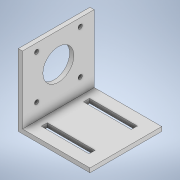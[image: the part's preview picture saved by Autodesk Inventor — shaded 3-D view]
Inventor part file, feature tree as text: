
AUTODESK INVENTOR PART (.ipt)
format: ipt  version: 2022 (Build 260153000, 153)  size: 141,312 bytes
history: native  units: mm
features: extrude x3, sketch x3
ambient origin geometry x8: Origin, YZ Plane, XZ Plane, XY Plane, X Axis, Y Axis, Z Axis, Center Point
bodies: Solid1 (feature_tree)
feature tree (6):
  extrude  "Extrusion1"  Depth=3.0mm
  extrude  "Extrusion2"  Depth=48.0mm
  extrude  "Extrusion3"  Depth=4.3mm
  sketch  "Sketch1"  dims[d0=51.0mm d1=3.0mm]
  sketch  "Sketch2"  dims[d2=48.0mm d3=48.0mm]
  sketch  "Sketch3"  dims[d4=51.0mm d5=0.0mm d7=22.0mm d12=3.0mm d13=3.0mm d14=51.0mm d15=0.0mm d16=12.865mm d17=2.15mm d18=9.0mm d20=7.85mm d21=270.0deg d22=2.15mm d23=4.3mm d24=0.0mm d25=0.0mm]
